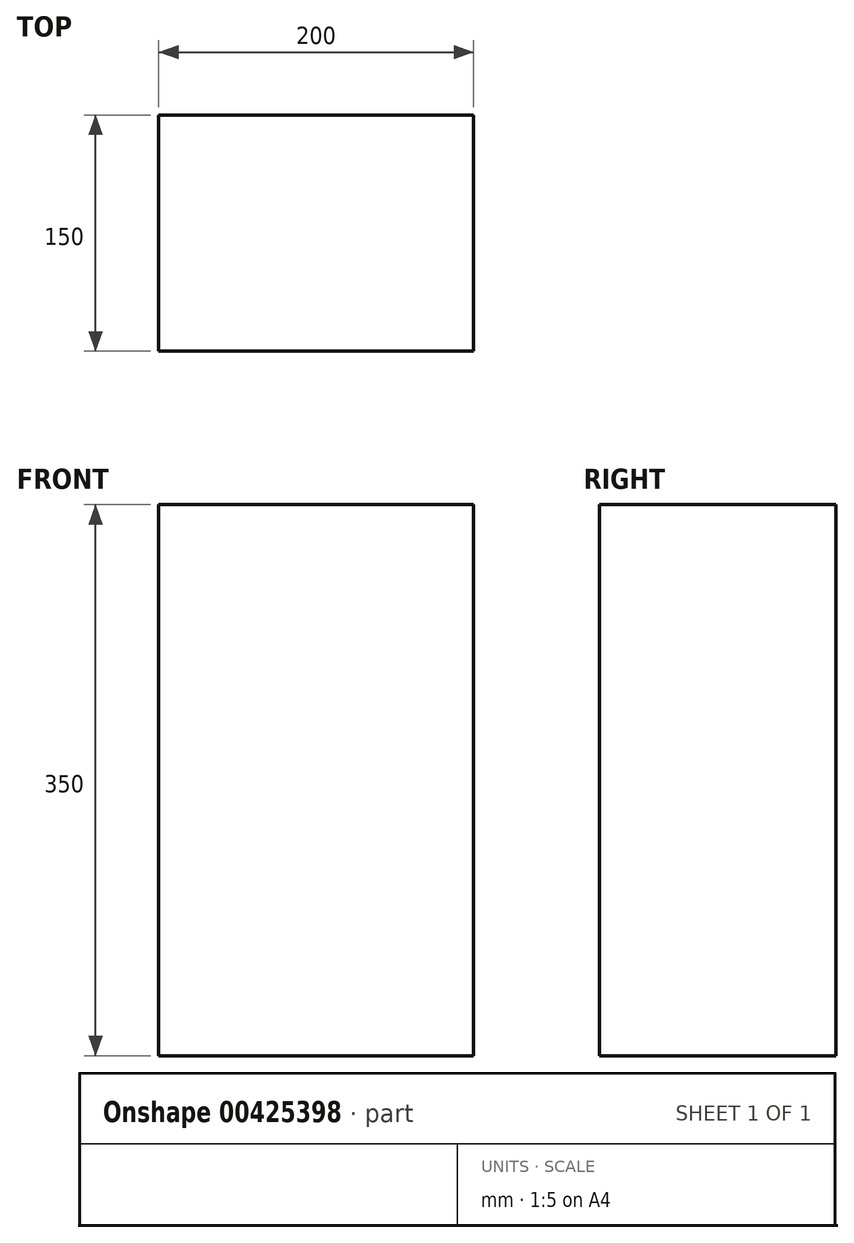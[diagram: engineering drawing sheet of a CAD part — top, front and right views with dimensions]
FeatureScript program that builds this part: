
annotation { "Feature Type Name" : "Feature", "Feature Type Description" : "" }
export const myFeature = defineFeature(function(context is Context, id is Id, definition is map)
    precondition{}
    {
        {
            assignVariable(context, id + "F0", {"name" : "HauteurMaxPetitRobot", "anyValue" : 350});
        }
        {
            var Q0;
            Q0=qCreatedBy(makeId("Top.planeOp"),FACE);
            var sketch = newSketch(context, id + "F1", { "sketchPlane" : qUnion([Q0])});
            skLineSegment(sketch, "E0.bottom", {"start": v(100, -75) * mm, "end": v(-100, -75) * mm});
            skLineSegment(sketch, "E0.top", {"start": v(100, 75) * mm, "end": v(-100, 75) * mm});
            skLineSegment(sketch, "E0.left", {"start": v(100, -75) * mm, "end": v(100, 75) * mm});
            skLineSegment(sketch, "E0.right", {"start": v(-100, -75) * mm, "end": v(-100, 75) * mm});
            skPoint(sketch, "E0.middle", {"position": v(0, 0) * mm});
            skSolve(sketch);
        }
        {
            var Q0;
            Q0=makeQuery(id+"F1.imprint","IMPRINT",FACE,{"disambiguationData":[TD([[makeQuery(id+"F1.imprint","IMPRINT",EDGE,{"derivedFrom":sQuery(id+"F1.wireOp",EDGE,"E0.bottom")}),-1.0]])]});
            extrude(context, id + "F2", {"entities" : qUnion([Q0]), "depth" : (getVariable(context, 'HauteurMaxPetitRobot')) * mm});
        }
    });
